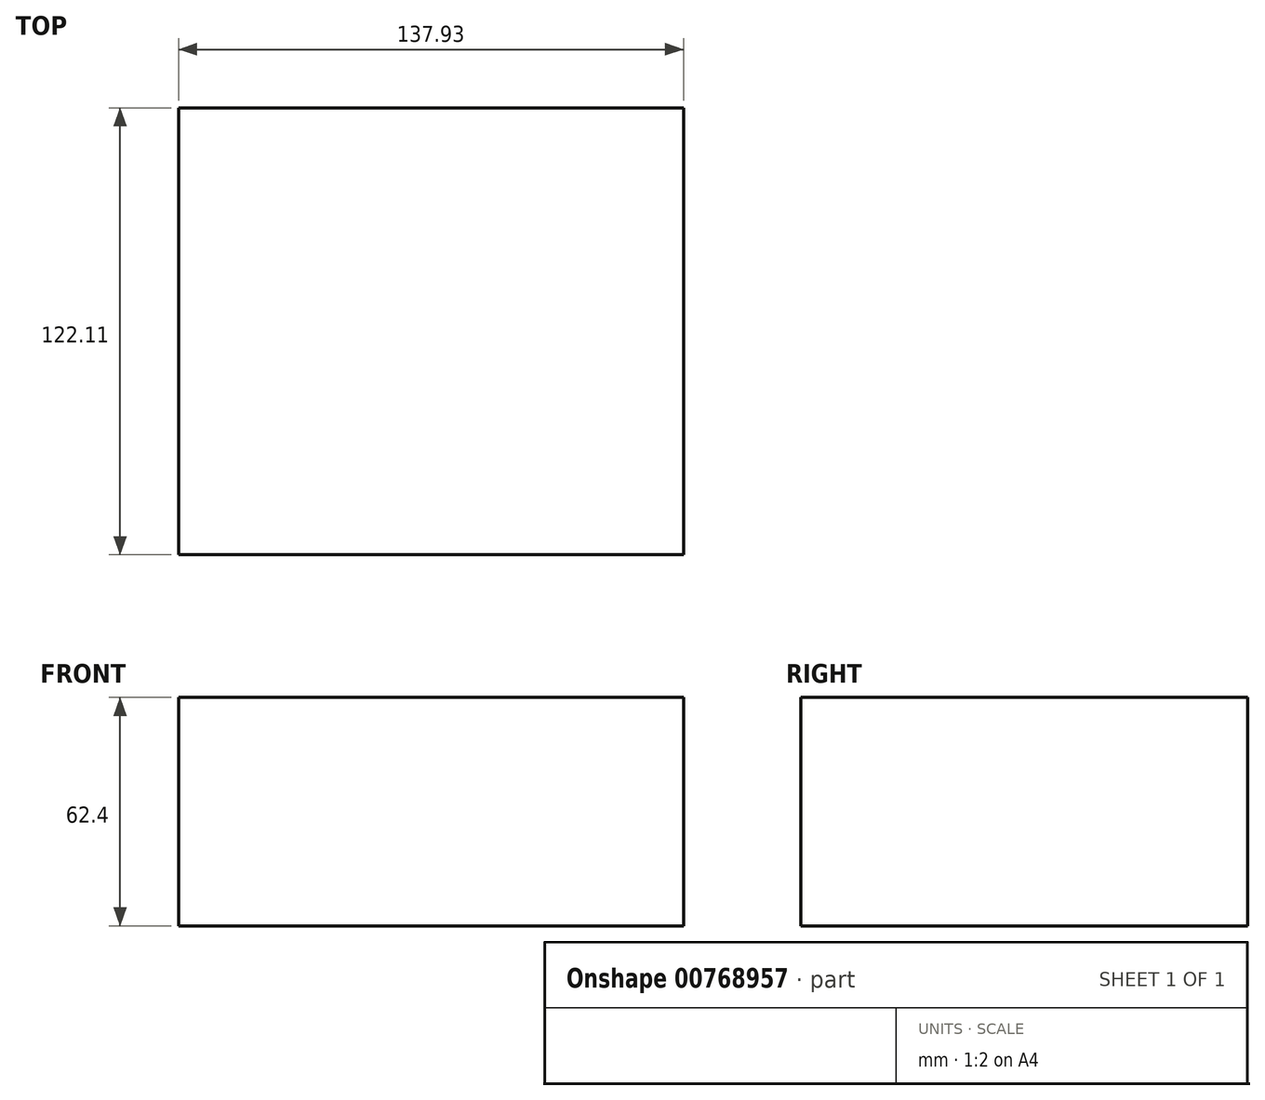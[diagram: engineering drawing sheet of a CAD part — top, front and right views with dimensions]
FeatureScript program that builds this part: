
annotation { "Feature Type Name" : "Feature", "Feature Type Description" : "" }
export const myFeature = defineFeature(function(context is Context, id is Id, definition is map)
    precondition{}
    {
        {
            var Q0;
            Q0=qCreatedBy(makeId("Right.planeOp"),FACE);
            var sketch = newSketch(context, id + "F0", { "sketchPlane" : qUnion([Q0])});
            skLineSegment(sketch, "E0", {"start": v(-74.94, 0) * mm, "end": v(-43.32, 0) * mm});
            skLineSegment(sketch, "E1", {"start": v(-43.32, 0) * mm, "end": v(47.17, 0) * mm});
            skLineSegment(sketch, "E2", {"start": v(47.17, 0) * mm, "end": v(47.17, 62.4) * mm});
            skLineSegment(sketch, "E3", {"start": v(47.17, 62.4) * mm, "end": v(-74.94, 62.4) * mm});
            skLineSegment(sketch, "E4", {"start": v(-74.94, 62.4) * mm, "end": v(-74.94, 0) * mm});
            skSolve(sketch);
        }
        {
            var Q0;
            Q0 = qSketchRegion(id + "F0", true);
            extrude(context, id + "F1", {"entities" : qUnion([Q0]), "depth" : 137.93 * mm, "offsetDistance" : 25.4 * mm});
        }
    });
